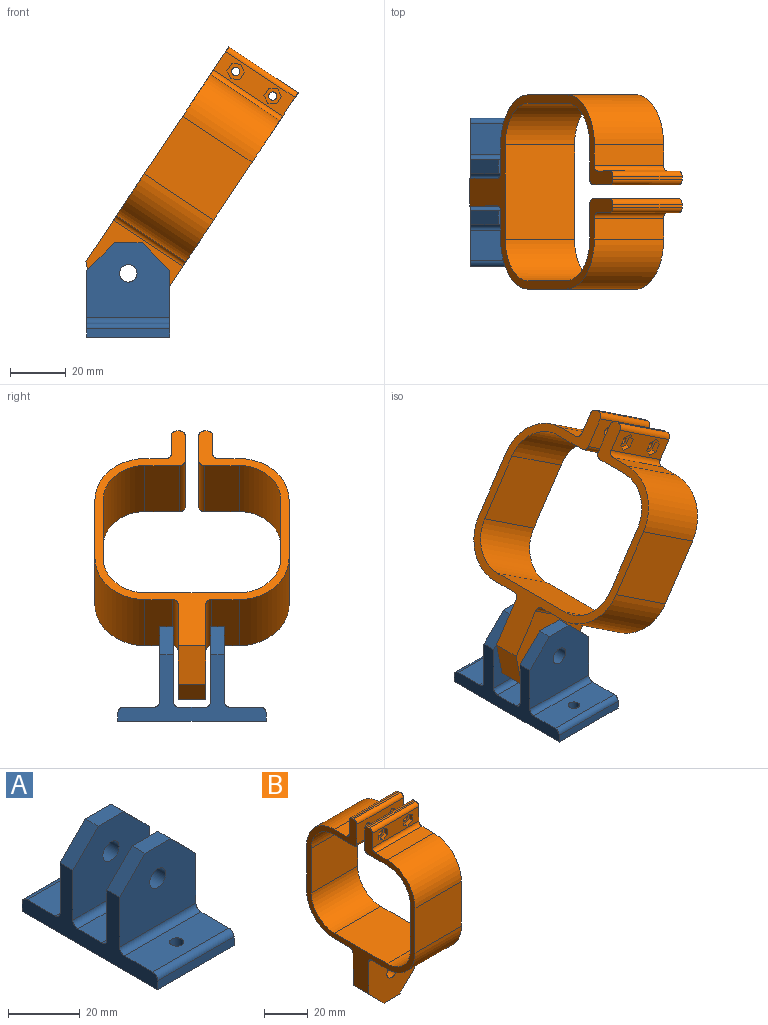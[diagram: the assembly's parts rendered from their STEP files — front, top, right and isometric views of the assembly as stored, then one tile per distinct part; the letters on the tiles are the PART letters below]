
ASSEMBLY  parts=2 mates=1
PART A: 28 faces, bbox 30x53.4x34 mm
  f0: plane 30x27mm, normal (0,1,0), area 678.3mm2, adj f1,f12,f13,f15,f18,f19,f25
  f1: plane 10x5mm, normal (0,0,1), area 50mm2, adj f0,f2,f18,f19
  f2: plane 30x27mm, normal (0,-1,0), area 678.3mm2, adj f1,f12,f13,f15,f18,f19,f20
  f3: plane 30x11mm, normal (0,0,1), area 317.4mm2, adj f12,f13,f20,f21,f27
  f4: plane 30x3mm, normal (0,-1,0), area 90mm2, adj f5,f12,f13,f21
  f5: plane 53.4x30mm, normal (0,0,-1), area 1576.9mm2, adj f4,f6,f12,f13,f26,f27
  f6: plane 30x3mm, normal (0,1,0), area 90mm2, adj f5,f12,f13,f22
  f7: plane 30x11mm, normal (0,0,1), area 317.4mm2, adj f12,f13,f22,f23,f26
  f8: plane 30x27mm, normal (0,1,0), area 678.3mm2, adj f9,f12,f13,f14,f16,f17,f23
  f9: plane 10x5mm, normal (0,0,1), area 50mm2, adj f8,f10,f16,f17
  f10: plane 30x27mm, normal (0,-1,0), area 678.3mm2, adj f9,f12,f13,f14,f16,f17,f24
  f11: plane 30x9.4mm, normal (0,0,1), area 282mm2, adj f12,f13,f24,f25
  f12: plane 53.4x24mm, normal (1,0,0), area 458.7mm2, adj f0,f2,f3,f4,f5,f6,f7,f8
  f13: plane 53.4x24mm, normal (-1,0,0), area 458.7mm2, adj f0,f2,f3,f4,f5,f6,f7,f8
  f14: cylinder r=3.17mm len=6.35mm, axis (0,1,0), area 99.7mm2, adj f8,f10
  f15: cylinder r=3.17mm len=6.35mm, axis (0,1,0), area 99.7mm2, adj f0,f2
  f16: plane 10x10mm, normal (0.71,0,0.71), area 70.7mm2, adj f8,f9,f10,f12
  f17: plane 10x10mm, normal (-0.71,0,0.71), area 70.7mm2, adj f8,f9,f10,f13
  f18: plane 10x10mm, normal (-0.71,0,0.71), area 70.7mm2, adj f0,f1,f2,f13
  f19: plane 10x10mm, normal (0.71,0,0.71), area 70.7mm2, adj f0,f1,f2,f12
  f20: cylinder r=2mm len=30mm, axis (1,0,0), area 94.2mm2, adj f2,f3,f12,f13
  f21: cylinder r=2mm len=30mm, axis (-1,0,0), area 94.2mm2, adj f3,f4,f12,f13
  f22: cylinder r=2mm len=30mm, axis (-1,0,0), area 94.2mm2, adj f6,f7,f12,f13
  f23: cylinder r=2mm len=30mm, axis (1,0,0), area 94.2mm2, adj f7,f8,f12,f13
  f24: cylinder r=2mm len=30mm, axis (1,0,0), area 94.2mm2, adj f10,f11,f12,f13
  f25: cylinder r=2mm len=30mm, axis (1,0,0), area 94.2mm2, adj f0,f11,f12,f13
  f26: cylinder r=2mm len=5mm, axis (0,0,1), area 62.8mm2, adj f5,f7
  f27: cylinder r=2mm len=5mm, axis (0,0,1), area 62.8mm2, adj f3,f5
PART B: 61 faces, bbox 30x70x103 mm
  f0: plane 30x12.5mm, normal (0,0,-1), area 375mm2, adj f20,f21,f22,f58
  f1: plane 30x25mm, normal (0,-1,0), area 750mm2, adj f20,f21,f22,f23
  f2: plane 34x30mm, normal (0,0,1), area 1020mm2, adj f20,f21,f23,f24
  f3: plane 30x25mm, normal (0,1,0), area 750mm2, adj f20,f21,f24,f25
  f4: plane 30x12.5mm, normal (0,0,-1), area 375mm2, adj f20,f21,f25,f49
  f5: plane 30x11mm, normal (0,1,0), area 315.9mm2, adj f20,f21,f44,f45,f49,f50
  f6: plane 30x1mm, normal (0,0,1), area 30mm2, adj f20,f21,f50,f51
  f7: plane 30x8mm, normal (0,-1,0), area 187.6mm2, adj f20,f21,f30,f31,f32,f33,f34,f35
  f8: plane 30x7.5mm, normal (0,0,1), area 225mm2, adj f20,f21,f26,f52
  f9: plane 30x25mm, normal (0,-1,0), area 750mm2, adj f20,f21,f26,f27
  f10: plane 30x10mm, normal (0,0,-1), area 300mm2, adj f20,f21,f27,f53
  f11: plane 30x28mm, normal (0,-1,0), area 708.3mm2, adj f12,f20,f21,f48,f53,f59,f60
  f12: plane 10x10mm, normal (0,0,-1), area 100mm2, adj f11,f13,f59,f60
  f13: plane 30x28mm, normal (0,1,0), area 708.3mm2, adj f12,f20,f21,f48,f54,f59,f60
  f14: plane 30x10mm, normal (0,0,-1), area 300mm2, adj f20,f21,f28,f54
  f15: plane 30x25mm, normal (0,1,0), area 750mm2, adj f20,f21,f28,f29
  f16: plane 30x7.5mm, normal (0,0,1), area 225mm2, adj f20,f21,f29,f55
  f17: plane 30x8mm, normal (0,1,0), area 225.9mm2, adj f20,f21,f46,f47,f55,f56
  f18: plane 30x1mm, normal (0,0,1), area 30mm2, adj f20,f21,f56,f57
  f19: plane 30x11mm, normal (0,-1,0), area 315.9mm2, adj f20,f21,f46,f47,f57,f58
  f20: plane 93x70mm, normal (1,0,0), area 968.3mm2, adj f0,f1,f2,f3,f4,f5,f6,f7
  f21: plane 93x70mm, normal (-1,0,0), area 968.3mm2, adj f0,f1,f2,f3,f4,f5,f6,f7
  f22: cylinder r=15mm len=30mm, axis (-1,0,0), area 706.9mm2, adj f0,f1,f20,f21
  f23: cylinder r=15mm len=30mm, axis (1,0,0), area 706.9mm2, adj f1,f2,f20,f21
  f24: cylinder r=15mm len=30mm, axis (-1,0,0), area 706.9mm2, adj f2,f3,f20,f21
  f25: cylinder r=15mm len=30mm, axis (1,0,0), area 706.9mm2, adj f3,f4,f20,f21
  f26: cylinder r=18mm len=30mm, axis (-1,0,0), area 848.2mm2, adj f8,f9,f20,f21
  f27: cylinder r=18mm len=30mm, axis (-1,0,0), area 848.2mm2, adj f9,f10,f20,f21
  f28: cylinder r=18mm len=30mm, axis (-1,0,0), area 848.2mm2, adj f14,f15,f20,f21
  f29: cylinder r=18mm len=30mm, axis (-1,0,0), area 848.2mm2, adj f15,f16,f20,f21
  f30: plane 2.75x2mm, normal (0.5,0,-0.87), area 6.4mm2, adj f7,f31,f35,f36
  f31: plane 3.18x2mm, normal (1,0,0), area 6.4mm2, adj f7,f30,f32,f36
  f32: plane 2.75x2mm, normal (0.5,0,0.87), area 6.4mm2, adj f7,f31,f33,f36
  f33: plane 2.75x2mm, normal (-0.5,0,0.87), area 6.4mm2, adj f7,f32,f34,f36
  f34: plane 3.18x2mm, normal (-1,0,0), area 6.4mm2, adj f7,f33,f35,f36
  f35: plane 2.75x2mm, normal (-0.5,0,-0.87), area 6.4mm2, adj f7,f30,f34,f36
  f36: plane 6.35x5.5mm, normal (0,-1,0), area 19.1mm2, adj f30,f31,f32,f33,f34,f35,f45
  f37: plane 2.75x2mm, normal (-0.5,0,0.87), area 6.4mm2, adj f7,f38,f42,f43
  f38: plane 3.18x2mm, normal (-1,0,0), area 6.4mm2, adj f7,f37,f39,f43
  f39: plane 2.75x2mm, normal (-0.5,0,-0.87), area 6.4mm2, adj f7,f38,f40,f43
  f40: plane 2.75x2mm, normal (0.5,0,-0.87), area 6.4mm2, adj f7,f39,f41,f43
  f41: plane 3.18x2mm, normal (1,0,0), area 6.4mm2, adj f7,f40,f42,f43
  f42: plane 2.75x2mm, normal (0.5,0,0.87), area 6.4mm2, adj f7,f37,f41,f43
  f43: plane 6.35x5.5mm, normal (0,-1,0), area 19.1mm2, adj f37,f38,f39,f40,f41,f42,f44
  f44: cylinder r=1.5mm len=3mm, axis (0,-1,0), area 28.3mm2, adj f5,f43
  f45: cylinder r=1.5mm len=3mm, axis (0,-1,0), area 28.3mm2, adj f5,f36
  f46: cylinder r=1.5mm len=5mm, axis (0,-1,0), area 47.1mm2, adj f17,f19
  f47: cylinder r=1.5mm len=5mm, axis (0,-1,0), area 47.1mm2, adj f17,f19
  f48: cylinder r=3.17mm len=10mm, axis (0,1,0), area 199.5mm2, adj f11,f13
  f49: cylinder r=2mm len=30mm, axis (1,0,0), area 94.2mm2, adj f4,f5,f20,f21
  f50: cylinder r=2mm len=30mm, axis (-1,0,0), area 94.2mm2, adj f5,f6,f20,f21
  f51: cylinder r=2mm len=30mm, axis (-1,0,0), area 94.2mm2, adj f6,f7,f20,f21
  f52: cylinder r=2mm len=30mm, axis (1,0,0), area 94.2mm2, adj f7,f8,f20,f21
  f53: cylinder r=2mm len=30mm, axis (1,0,0), area 94.2mm2, adj f10,f11,f20,f21
  f54: cylinder r=2mm len=30mm, axis (1,0,0), area 94.2mm2, adj f13,f14,f20,f21
  f55: cylinder r=2mm len=30mm, axis (-1,0,0), area 94.2mm2, adj f16,f17,f20,f21
  f56: cylinder r=2mm len=30mm, axis (-1,0,0), area 94.2mm2, adj f17,f18,f20,f21
  f57: cylinder r=2mm len=30mm, axis (-1,0,0), area 94.2mm2, adj f18,f19,f20,f21
  f58: cylinder r=2mm len=30mm, axis (-1,0,0), area 94.2mm2, adj f0,f19,f20,f21
  f59: plane 10x10mm, normal (-0.71,0,-0.71), area 141.4mm2, adj f11,f12,f13,f21
  f60: plane 10x10mm, normal (0.71,0,-0.71), area 141.4mm2, adj f11,f12,f13,f20
PLACE A t=(-15.35,0.02,13.33)mm fixed
PLACE B rot(axis=(0,1,0),33.6deg) t=(12.34,0.02,14.03)mm
MATE revolute B.f48 <-> A.f14  axis (0,1,0) through (-0.35,5.02,-32.17)mm
